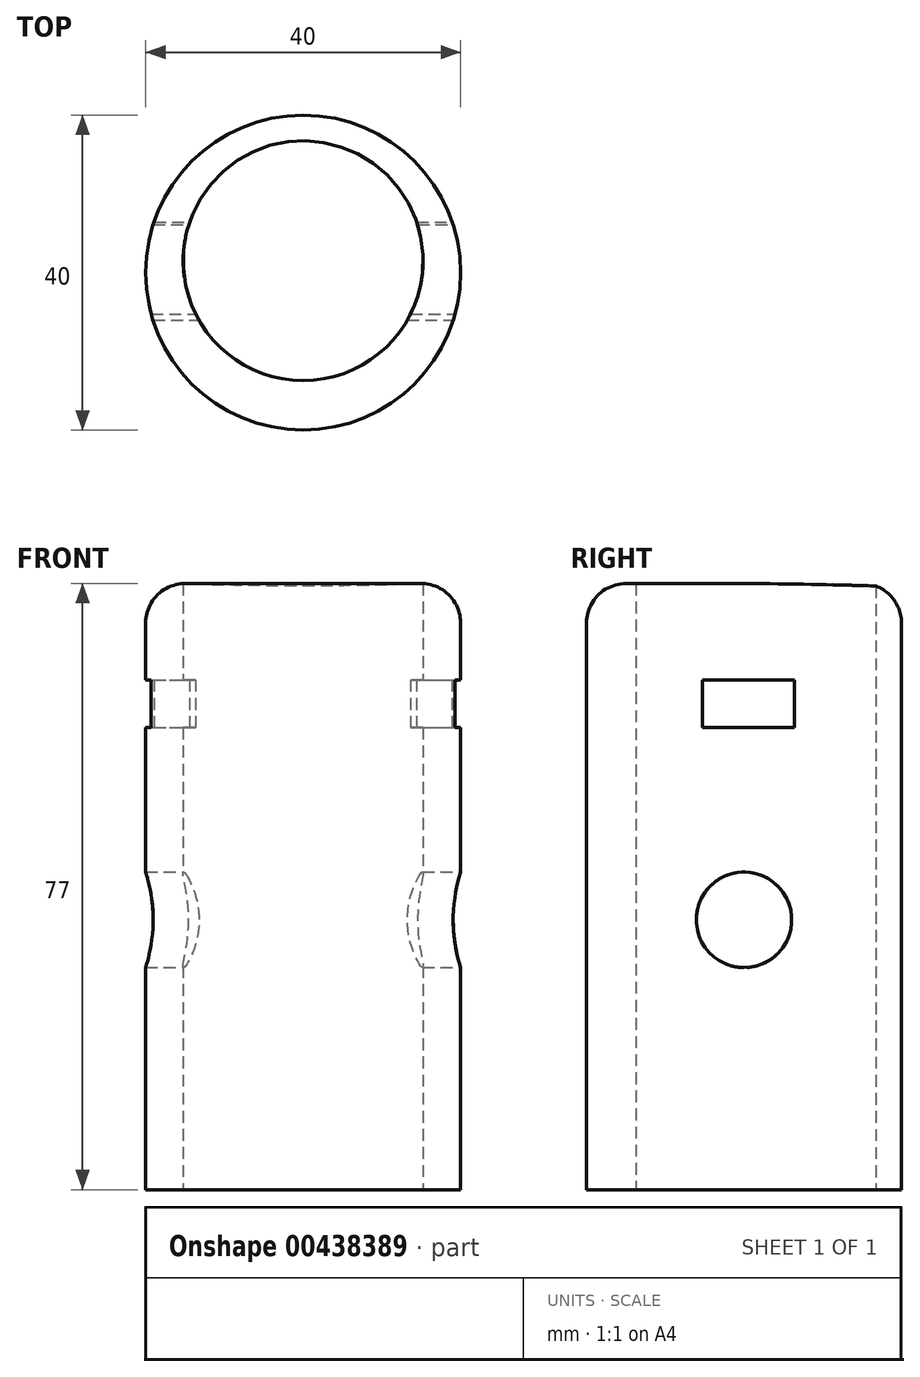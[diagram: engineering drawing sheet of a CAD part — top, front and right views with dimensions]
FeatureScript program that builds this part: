
annotation { "Feature Type Name" : "Feature", "Feature Type Description" : "" }
export const myFeature = defineFeature(function(context is Context, id is Id, definition is map)
    precondition{}
    {
        {
            var Q0;
            Q0=qCreatedBy(makeId("Top.planeOp"),FACE);
            var sketch = newSketch(context, id + "F0", { "sketchPlane" : qUnion([Q0])});
            skCircle(sketch, "E0", {"center": v(0, 0) * mm, "radius": 20 * mm});
            skCircle(sketch, "E1", {"center": v(0, 1.51) * mm, "radius": 15.24 * mm});
            skSolve(sketch);
        }
        {
            var Q0;
            Q0=makeQuery(id+"F0.imprint","IMPRINT",FACE,{"disambiguationData":[TD([[makeQuery(id+"F0.imprint","IMPRINT",EDGE,{"derivedFrom":sQuery(id+"F0.wireOp",EDGE,"E0")}),1.0]])]});
            extrude(context, id + "F1", {"entities" : qUnion([Q0]), "depth" : 77 * mm});
        }
        {
            var Q0;
            Q0=makeQuery(id+"F1.opExtrude","CAP_EDGE",EDGE,{"disambiguationData":[OSD([sQuery(id+"F0.wireOp",EDGE,"E0")])],"isStart":false});
            fillet(context, id + "F2", {"entities" : qUnion([Q0]), "radius" : 5 * mm, "tangentPropagation" : true, "allowEdgeOverflow" : false});
        }
        {
            var Q0;
            Q0=qCreatedBy(makeId("Right.planeOp"),FACE);
            var sketch = newSketch(context, id + "F3", { "sketchPlane" : qUnion([Q0])});
            skCircle(sketch, "E2", {"center": v(0, 34.28) * mm, "radius": 6.07 * mm});
            skLineSegment(sketch, "E3.bottom", {"start": v(-5.25, 64.76) * mm, "end": v(6.44, 64.76) * mm});
            skLineSegment(sketch, "E3.top", {"start": v(-5.25, 58.7) * mm, "end": v(6.44, 58.7) * mm});
            skLineSegment(sketch, "E3.left", {"start": v(-5.25, 64.76) * mm, "end": v(-5.25, 58.7) * mm});
            skLineSegment(sketch, "E3.right", {"start": v(6.44, 64.76) * mm, "end": v(6.44, 58.7) * mm});
            skSolve(sketch);
        }
        {
            var Q0;
            Q0=makeQuery(id+"F3.imprint","IMPRINT",FACE,{"disambiguationData":[TD([[makeQuery(id+"F3.imprint","IMPRINT",EDGE,{"derivedFrom":sQuery(id+"F3.wireOp",EDGE,"E2")}),1.0]])]});
            extrude(context, id + "F4", {"entities" : qUnion([Q0]), "operationType" : NewBodyOperationType.ADD, "depth" : 25 * mm, "hasSecondDirection" : true, "secondDirectionOppositeDirection" : true, "secondDirectionDepth" : 25 * mm});
        }
        {
            var Q0;
            Q0 = qSketchRegion(id + "F3", true);
            extrude(context, id + "F5", {"entities" : qUnion([Q0]), "operationType" : NewBodyOperationType.REMOVE, "oppositeDirection" : true, "depth" : 25 * mm, "hasSecondDirection" : true, "secondDirectionOppositeDirection" : false, "secondDirectionDepth" : 25 * mm});
        }
    });
